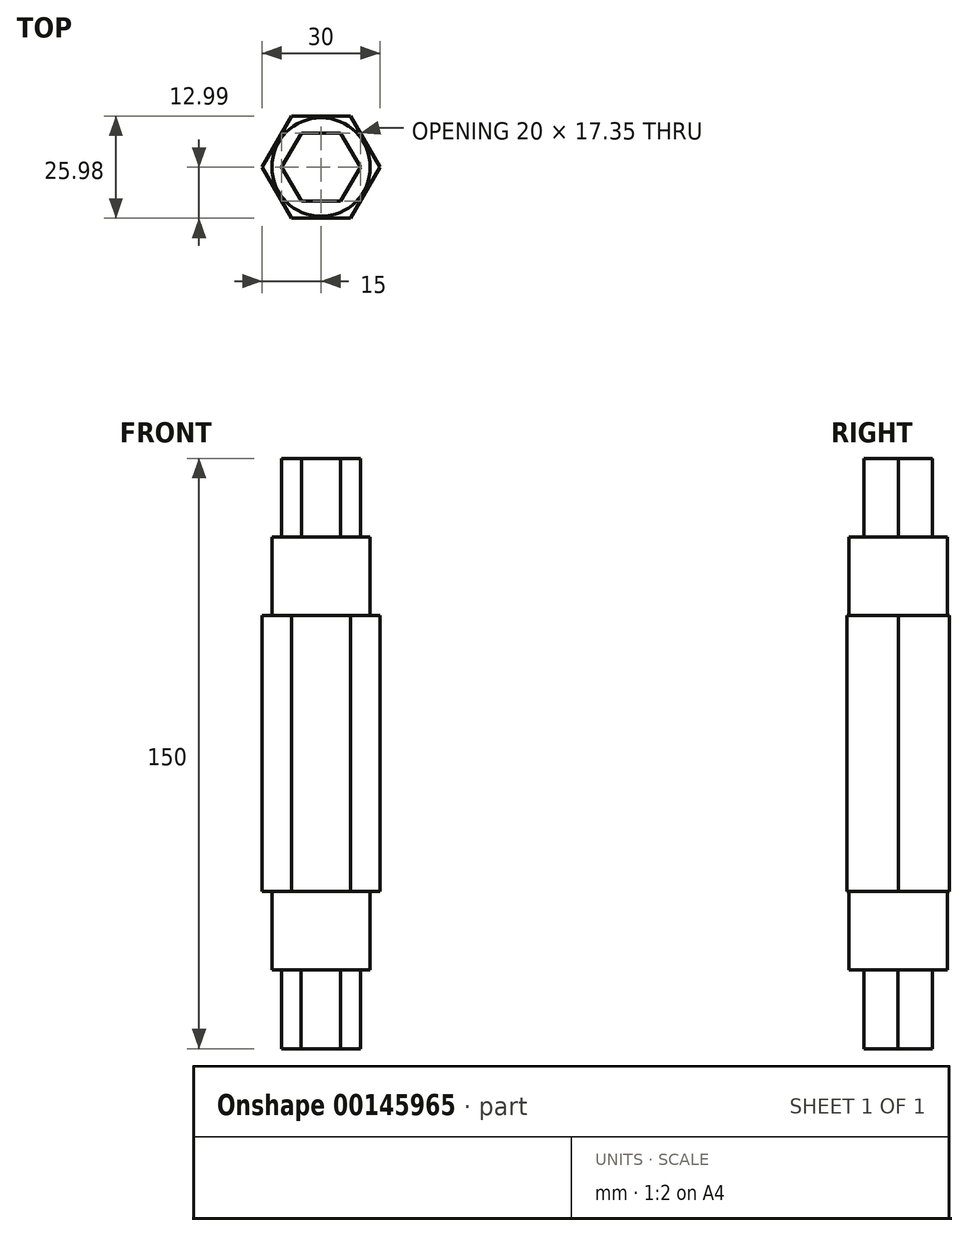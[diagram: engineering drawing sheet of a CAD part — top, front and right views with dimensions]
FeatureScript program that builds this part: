
annotation { "Feature Type Name" : "Feature", "Feature Type Description" : "" }
export const myFeature = defineFeature(function(context is Context, id is Id, definition is map)
    precondition{}
    {
        {
            var Q0;
            Q0=qCreatedBy(makeId("Top.planeOp"),FACE);
            var sketch = newSketch(context, id + "F0", { "sketchPlane" : qUnion([Q0])});
            skCircle(sketch, "E0.cCircle", {"center": v(0, 0) * mm, "radius": 13 * mm, "construction": true});
            skLineSegment(sketch, "E0.0", {"start": v(-15, 0) * mm, "end": v(-7.5, 13) * mm});
            skLineSegment(sketch, "E0.1", {"start": v(-7.5, 13) * mm, "end": v(7.5, 13) * mm});
            skLineSegment(sketch, "E0.2", {"start": v(7.5, 13) * mm, "end": v(15, 0) * mm});
            skLineSegment(sketch, "E0.3", {"start": v(15, 0) * mm, "end": v(7.5, -13) * mm});
            skLineSegment(sketch, "E0.4", {"start": v(7.5, -13) * mm, "end": v(-7.5, -13) * mm});
            skLineSegment(sketch, "E0.5", {"start": v(-7.5, -13) * mm, "end": v(-15, 0) * mm});
            skPoint(sketch, "E0.0.midPoint", {"position": v(-11.25, 6.5) * mm});
            skSolve(sketch);
        }
        {
            var Q0;
            Q0=makeQuery(id+"F0.imprint","IMPRINT",FACE,{"disambiguationData":[TD([[makeQuery(id+"F0.imprint","IMPRINT",EDGE,{"derivedFrom":sQuery(id+"F0.wireOp",EDGE,"E0.0")}),-1.0]])]});
            extrude(context, id + "F1", {"entities" : qUnion([Q0]), "depth" : 70 * mm});
        }
        {
            var Q0;
            Q0=makeQuery(id+"F1.opExtrude","CAP_FACE",FACE,{"disambiguationData":[OSD([sQuery(id+"F0.wireOp",EDGE,"E0.0"),sQuery(id+"F0.wireOp",EDGE,"E0.1"),sQuery(id+"F0.wireOp",EDGE,"E0.2"),sQuery(id+"F0.wireOp",EDGE,"E0.3"),sQuery(id+"F0.wireOp",EDGE,"E0.4"),sQuery(id+"F0.wireOp",EDGE,"E0.5")])],"isStart":false});
            var sketch = newSketch(context, id + "F2", { "sketchPlane" : qUnion([Q0])});
            skCircle(sketch, "E1", {"center": v(0, 0) * mm, "radius": 12.5 * mm});
            skSolve(sketch);
        }
        {
            var Q0;
            Q0=makeQuery(id+"F2.imprint","IMPRINT",FACE,{"disambiguationData":[TD([[makeQuery(id+"F2.imprint","IMPRINT",EDGE,{"derivedFrom":sQuery(id+"F2.wireOp",EDGE,"E1")}),1.0]])]});
            extrude(context, id + "F3", {"entities" : qUnion([Q0]), "operationType" : NewBodyOperationType.ADD, "depth" : 20 * mm});
        }
        {
            var Q0;
            Q0=makeQuery(id+"F1.opExtrude","CAP_FACE",FACE,{"disambiguationData":[OSD([sQuery(id+"F0.wireOp",EDGE,"E0.0"),sQuery(id+"F0.wireOp",EDGE,"E0.1"),sQuery(id+"F0.wireOp",EDGE,"E0.2"),sQuery(id+"F0.wireOp",EDGE,"E0.3"),sQuery(id+"F0.wireOp",EDGE,"E0.4"),sQuery(id+"F0.wireOp",EDGE,"E0.5")])],"isStart":true});
            var sketch = newSketch(context, id + "F4", { "sketchPlane" : qUnion([Q0])});
            skCircle(sketch, "E2", {"center": v(0, 0) * mm, "radius": 12.5 * mm});
            skSolve(sketch);
        }
        {
            var Q0;
            Q0=makeQuery(id+"F4.imprint","IMPRINT",FACE,{"disambiguationData":[TD([[makeQuery(id+"F4.imprint","IMPRINT",EDGE,{"derivedFrom":sQuery(id+"F4.wireOp",EDGE,"E2")}),1.0]])]});
            extrude(context, id + "F5", {"entities" : qUnion([Q0]), "operationType" : NewBodyOperationType.ADD, "depth" : 20 * mm});
        }
        {
            var Q0;
            Q0=makeQuery(id+"F3.opExtrude","CAP_FACE",FACE,{"disambiguationData":[OSD([sQuery(id+"F2.wireOp",EDGE,"E1")])],"isStart":false});
            var sketch = newSketch(context, id + "F6", { "sketchPlane" : qUnion([Q0])});
            skCircle(sketch, "E3.cCircle", {"center": v(0, 0) * mm, "radius": 8.66 * mm, "construction": true});
            skLineSegment(sketch, "E3.0", {"start": v(-5, 8.66) * mm, "end": v(5, 8.66) * mm});
            skLineSegment(sketch, "E3.1", {"start": v(5, 8.66) * mm, "end": v(10, 0) * mm});
            skLineSegment(sketch, "E3.2", {"start": v(10, 0) * mm, "end": v(5, -8.66) * mm});
            skLineSegment(sketch, "E3.3", {"start": v(5, -8.66) * mm, "end": v(-5, -8.66) * mm});
            skLineSegment(sketch, "E3.4", {"start": v(-5, -8.66) * mm, "end": v(-10, 0) * mm});
            skLineSegment(sketch, "E3.5", {"start": v(-10, 0) * mm, "end": v(-5, 8.66) * mm});
            skPoint(sketch, "E3.0.midPoint", {"position": v(0, 8.66) * mm});
            skSolve(sketch);
        }
        {
            var Q0;
            Q0=makeQuery(id+"F6.imprint","IMPRINT",FACE,{"disambiguationData":[TD([[makeQuery(id+"F6.imprint","IMPRINT",EDGE,{"derivedFrom":sQuery(id+"F6.wireOp",EDGE,"E3.0")}),-1.0]])]});
            extrude(context, id + "F7", {"entities" : qUnion([Q0]), "operationType" : NewBodyOperationType.ADD, "depth" : 20 * mm});
        }
        {
            var Q0;
            Q0=makeQuery(id+"F5.opExtrude","CAP_FACE",FACE,{"disambiguationData":[OSD([sQuery(id+"F4.wireOp",EDGE,"E2")])],"isStart":false});
            var sketch = newSketch(context, id + "F8", { "sketchPlane" : qUnion([Q0])});
            skCircle(sketch, "E4.cCircle", {"center": v(0, 0) * mm, "radius": 8.66 * mm, "construction": true});
            skLineSegment(sketch, "E4.0", {"start": v(4.97, 8.68) * mm, "end": v(10, 0.03) * mm});
            skLineSegment(sketch, "E4.1", {"start": v(10, 0.03) * mm, "end": v(5.03, -8.64) * mm});
            skLineSegment(sketch, "E4.2", {"start": v(5.03, -8.64) * mm, "end": v(-4.97, -8.68) * mm});
            skLineSegment(sketch, "E4.3", {"start": v(-4.97, -8.68) * mm, "end": v(-10, -0.03) * mm});
            skLineSegment(sketch, "E4.4", {"start": v(-10, -0.03) * mm, "end": v(-5.03, 8.64) * mm});
            skLineSegment(sketch, "E4.5", {"start": v(-5.03, 8.64) * mm, "end": v(4.97, 8.68) * mm});
            skPoint(sketch, "E4.0.midPoint", {"position": v(7.49, 4.35) * mm});
            skSolve(sketch);
        }
        {
            var Q0;
            Q0=makeQuery(id+"F8.imprint","IMPRINT",FACE,{"disambiguationData":[TD([[makeQuery(id+"F8.imprint","IMPRINT",EDGE,{"derivedFrom":sQuery(id+"F8.wireOp",EDGE,"E4.0")}),-1.0]])]});
            extrude(context, id + "F9", {"entities" : qUnion([Q0]), "operationType" : NewBodyOperationType.ADD, "depth" : 20 * mm});
        }
    });
